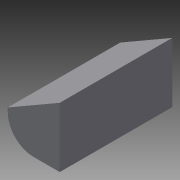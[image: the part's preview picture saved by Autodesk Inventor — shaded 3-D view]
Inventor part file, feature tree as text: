
AUTODESK INVENTOR PART (.ipt)
format: ipt  version: 2015 SP1 (Build 190203100, 203)  size: 75,264 bytes
history: native  units: in
note: dims shown in document units (in); Inventor stores cm internally (conversion verified against a paired STEP export)
features: extrude x1, sketch x1
ambient origin geometry x8: Origin, YZ Plane, XZ Plane, XY Plane, X Axis, Y Axis, Z Axis, Center Point
bodies: Solid1 (feature_tree)
feature tree (2):
  extrude  "Extrusion1"  TaperAngle=60.0deg  [1 undecoded]
  sketch  "Sketch1"  dims[d1=8.0in d2=60.0deg d3=8.0in d4=3.5in d5=15.0in d6=0.0in]
note: 1 required parameter value undecoded (feature->parameter linkage not recoverable at this tier; creation-order binding heuristic only, values carry confidence <= 0.55)
